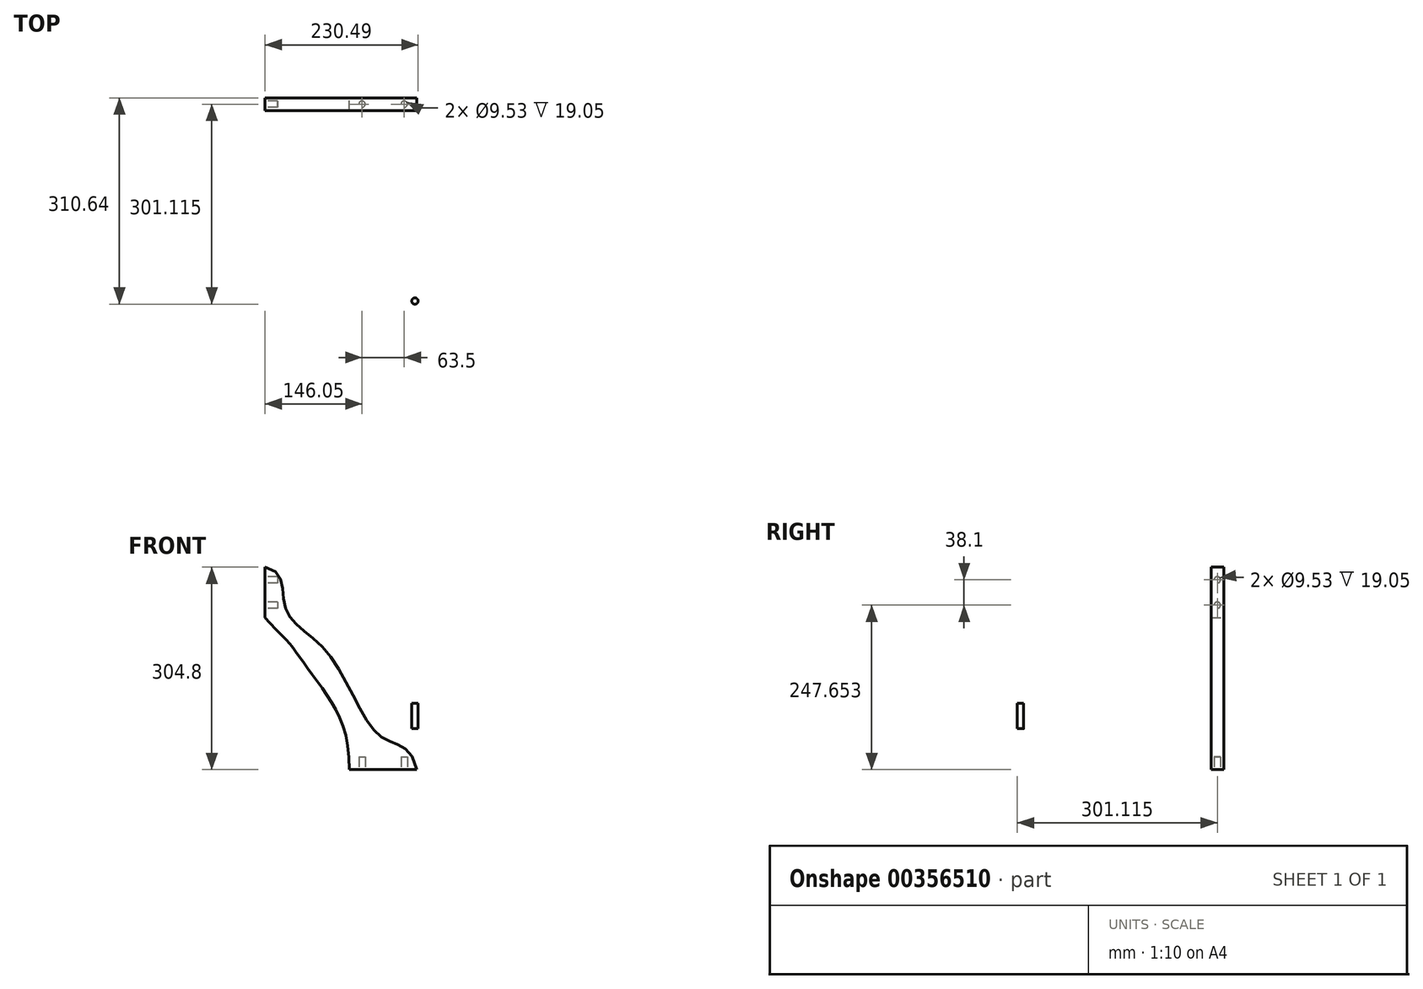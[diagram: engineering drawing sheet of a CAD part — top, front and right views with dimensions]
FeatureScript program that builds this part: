
annotation { "Feature Type Name" : "Feature", "Feature Type Description" : "" }
export const myFeature = defineFeature(function(context is Context, id is Id, definition is map)
    precondition{}
    {
        {
            assignVariable(context, id + "F0", {"name" : "BraceThickness", "anyValue" : 19.05 * mm});
        }
        {
            var Q0;
            Q0=qCreatedBy(makeId("Front.planeOp"),FACE);
            var sketch = newSketch(context, id + "F1", { "sketchPlane" : qUnion([Q0])});
            skLineSegment(sketch, "E0.bottom", {"start": v(-59.03, 243) * mm, "end": v(169.57, 243) * mm, "construction": true});
            skLineSegment(sketch, "E0.top", {"start": v(-59.03, -61.8) * mm, "end": v(169.57, -61.8) * mm, "construction": true});
            skLineSegment(sketch, "E0.left", {"start": v(-59.03, 243) * mm, "end": v(-59.03, -61.8) * mm, "construction": true});
            skLineSegment(sketch, "E0.right", {"start": v(169.57, 243) * mm, "end": v(169.57, -61.8) * mm, "construction": true});
            skLineSegment(sketch, "E1", {"start": v(-59.03, 243) * mm, "end": v(-59.03, 166.8) * mm});
            skLineSegment(sketch, "E2", {"start": v(169.57, -61.8) * mm, "end": v(67.97, -61.8) * mm});
            skFitSpline(sketch, "E3", {"points": [v(-59.03, 243) * mm, v(-28.87, 182.63) * mm, v(35.82, 113.2) * mm, v(115.17, -11.84) * mm, v(169.57, -61.8) * mm], "startDerivative": vector(472.1, -84.93) * mm, "endDerivative": vector(127.88, -576.62) * mm});
            skFitSpline(sketch, "E4", {"points": [v(-59.03, 166.8) * mm, v(-18.5, 123.5) * mm, v(21.22, 68.73) * mm, v(67.97, -61.8) * mm], "startDerivative": vector(437.3, -467.24) * mm, "endDerivative": vector(-4.72, -456.2) * mm});
            skSolve(sketch);
        }
        {
            var Q0;
            Q0 = qSketchRegion(id + "F1", true);
            extrude(context, id + "F2", {"entities" : qUnion([Q0]), "depth" : getVariable(context, 'BraceThickness')});
        }
        {
            var Q0;
            Q0=makeQuery(id+"F2.opExtrude","SWEPT_FACE",FACE,{"disambiguationData":[OSD([sQuery(id+"F1.wireOp",EDGE,"E1")])]});
            var sketch = newSketch(context, id + "F3", { "sketchPlane" : qUnion([Q0])});
            skLineSegment(sketch, "E5", {"start": v(9.53, 243) * mm, "end": v(9.53, 166.8) * mm, "construction": true});
            skCircle(sketch, "E6", {"center": v(9.53, 223.95) * mm, "radius": 4.76 * mm});
            skCircle(sketch, "E7", {"center": v(9.53, 185.85) * mm, "radius": 4.76 * mm});
            skSolve(sketch);
        }
        {
            var Q0;
            Q0 = qSketchRegion(id + "F3", true);
            extrude(context, id + "F4", {"entities" : qUnion([Q0]), "operationType" : NewBodyOperationType.REMOVE, "oppositeDirection" : true, "depth" : 19.05 * mm});
        }
        {
            var Q0;
            Q0=makeQuery(id+"F2.opExtrude","SWEPT_FACE",FACE,{"disambiguationData":[OSD([sQuery(id+"F1.wireOp",EDGE,"E2")])]});
            var sketch = newSketch(context, id + "F5", { "sketchPlane" : qUnion([Q0])});
            skLineSegment(sketch, "E8", {"start": v(67.97, 9.53) * mm, "end": v(169.57, 9.53) * mm, "construction": true});
            skCircle(sketch, "E9", {"center": v(150.52, 9.53) * mm, "radius": 4.76 * mm});
            skCircle(sketch, "E10", {"center": v(87.02, 9.53) * mm, "radius": 4.76 * mm});
            skSolve(sketch);
        }
        {
            var Q0;
            Q0 = qSketchRegion(id + "F5", true);
            extrude(context, id + "F6", {"entities" : qUnion([Q0]), "operationType" : NewBodyOperationType.REMOVE, "oppositeDirection" : true, "depth" : 19.05 * mm});
        }
        {
            var Q0;
            Q0=qCreatedBy(makeId("Top.planeOp"),FACE);
            var sketch = newSketch(context, id + "F7", { "sketchPlane" : qUnion([Q0])});
            skCircle(sketch, "E11", {"center": v(166.7, -305.88) * mm, "radius": 4.76 * mm});
            skSolve(sketch);
        }
        {
            var Q0;
            Q0 = qSketchRegion(id + "F7", true);
            extrude(context, id + "F8", {"entities" : qUnion([Q0]), "depth" : 38.1 * mm});
        }
    });
